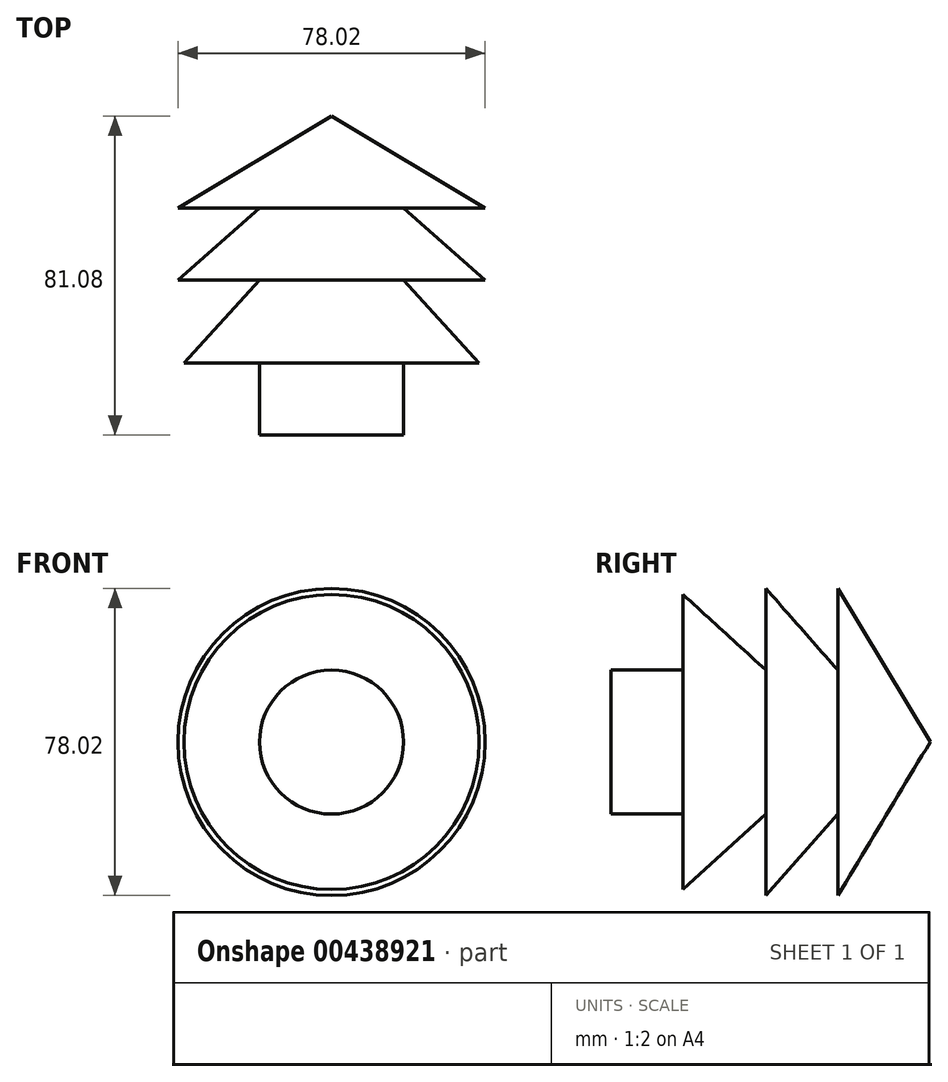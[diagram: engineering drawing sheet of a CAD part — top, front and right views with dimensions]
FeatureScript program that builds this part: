
annotation { "Feature Type Name" : "Feature", "Feature Type Description" : "" }
export const myFeature = defineFeature(function(context is Context, id is Id, definition is map)
    precondition{}
    {
        {
            var Q0;
            Q0=qCreatedBy(makeId("Top.planeOp"),FACE);
            var sketch = newSketch(context, id + "F0", { "sketchPlane" : qUnion([Q0])});
            skLineSegment(sketch, "E0", {"start": v(0, 46.18) * mm, "end": v(0, -34.9) * mm});
            skLineSegment(sketch, "E1", {"start": v(0, -34.9) * mm, "end": v(18.29, -34.9) * mm});
            skLineSegment(sketch, "E2", {"start": v(18.29, -34.9) * mm, "end": v(18.29, -16.61) * mm});
            skLineSegment(sketch, "E3", {"start": v(18.29, -16.61) * mm, "end": v(37.5, -16.61) * mm});
            skLineSegment(sketch, "E4", {"start": v(37.5, -16.61) * mm, "end": v(18.29, 4.42) * mm});
            skLineSegment(sketch, "E5", {"start": v(18.29, 4.42) * mm, "end": v(39.01, 4.42) * mm});
            skLineSegment(sketch, "E6", {"start": v(39.01, 4.42) * mm, "end": v(18.29, 22.7) * mm});
            skLineSegment(sketch, "E7", {"start": v(18.29, 22.7) * mm, "end": v(39.01, 22.7) * mm});
            skLineSegment(sketch, "E8", {"start": v(39.01, 22.7) * mm, "end": v(0, 46.18) * mm});
            skLineSegment(sketch, "E9", {"start": v(0, 55.63) * mm, "end": v(0, -50.14) * mm});
            skSolve(sketch);
        }
        {
            var Q0;
            Q0 = qSketchRegion(id + "F0", true);
            var Q1;
            Q1=sQuery(id+"F0.wireOp",EDGE,"E9");
            revolve(context, id + "F1", {"entities" : qUnion([Q0]), "axis" : qUnion([Q1]), "revolveType" : RevolveType.FULL});
        }
    });
